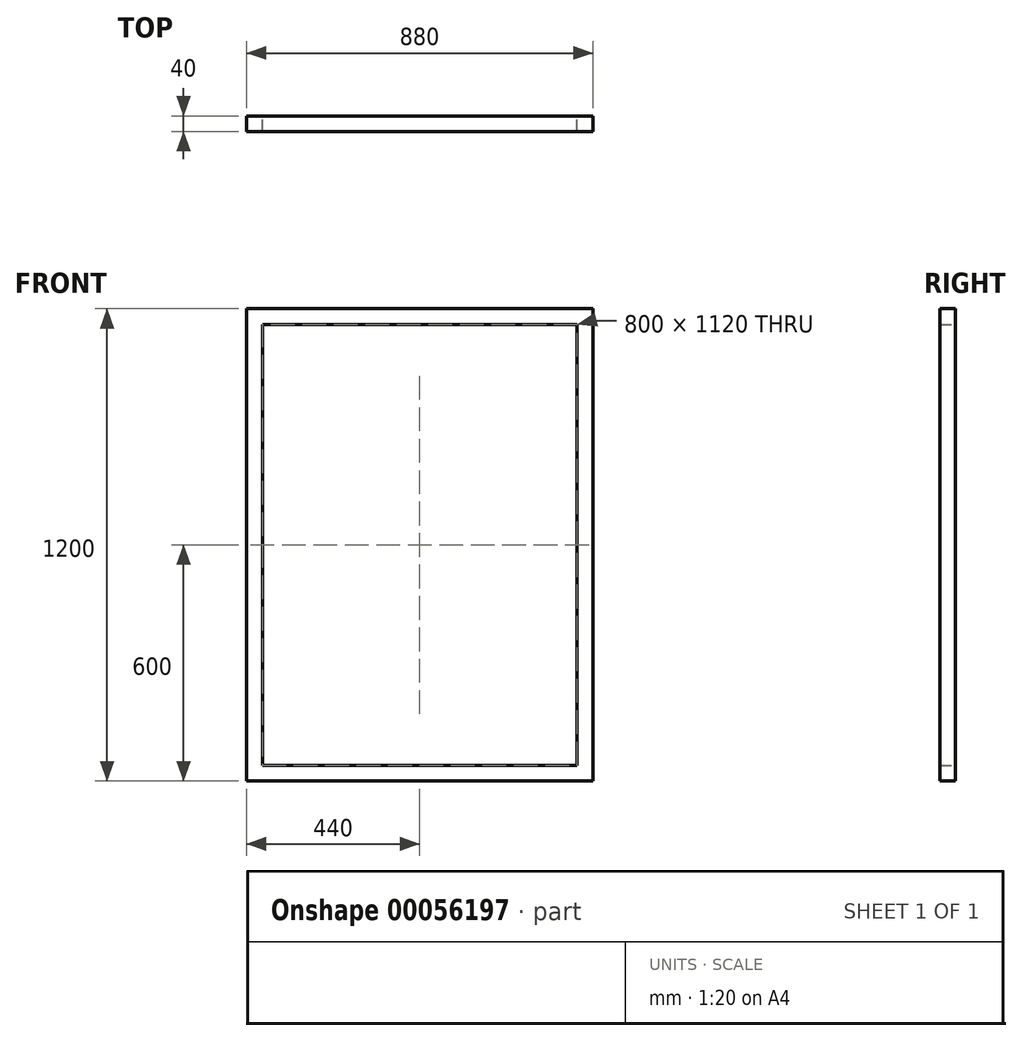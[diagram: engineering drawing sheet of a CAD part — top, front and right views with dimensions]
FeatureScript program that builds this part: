
annotation { "Feature Type Name" : "Feature", "Feature Type Description" : "" }
export const myFeature = defineFeature(function(context is Context, id is Id, definition is map)
    precondition{}
    {
        {
            var Q0;
            Q0=qCreatedBy(makeId("Front.planeOp"),FACE);
            var sketch = newSketch(context, id + "F0", { "sketchPlane" : qUnion([Q0])});
            skLineSegment(sketch, "E0.rect.bottom", {"start": v(440, -600) * mm, "end": v(-440, -600) * mm});
            skLineSegment(sketch, "E0.rect.top", {"start": v(440, 600) * mm, "end": v(-440, 600) * mm});
            skLineSegment(sketch, "E0.rect.left", {"start": v(440, -600) * mm, "end": v(440, 600) * mm});
            skLineSegment(sketch, "E0.rect.right", {"start": v(-440, -600) * mm, "end": v(-440, 600) * mm});
            skPoint(sketch, "E0.rect.middle", {"position": v(0, 0) * mm});
            skLineSegment(sketch, "E1.rect.bottom", {"start": v(400, 560) * mm, "end": v(-400, 560) * mm});
            skLineSegment(sketch, "E1.rect.top", {"start": v(400, -560) * mm, "end": v(-400, -560) * mm});
            skLineSegment(sketch, "E1.rect.left", {"start": v(400, 560) * mm, "end": v(400, -560) * mm});
            skLineSegment(sketch, "E1.rect.right", {"start": v(-400, 560) * mm, "end": v(-400, -560) * mm});
            skSolve(sketch);
        }
        {
            var Q0;
            Q0=makeQuery(id+"F0.imprint","IMPRINT",FACE,{"disambiguationData":[TD([[makeQuery(id+"F0.imprint","IMPRINT",EDGE,{"derivedFrom":sQuery(id+"F0.wireOp",EDGE,"E0.rect.bottom")}),-1.0]])]});
            extrude(context, id + "F1", {"entities" : qUnion([Q0]), "depth" : 40 * mm});
        }
    });
